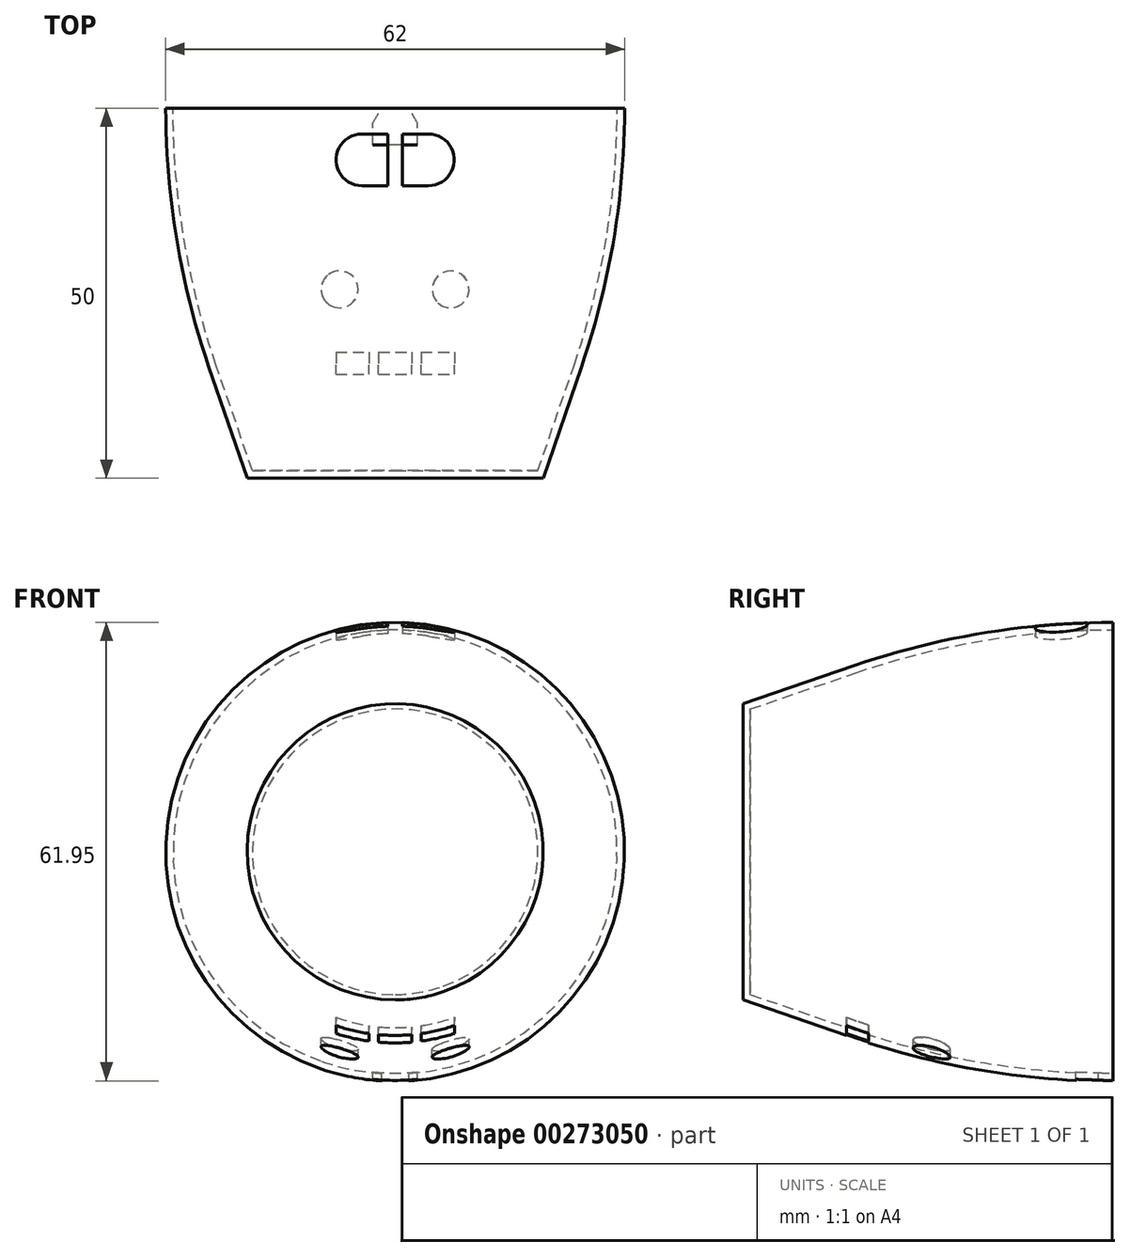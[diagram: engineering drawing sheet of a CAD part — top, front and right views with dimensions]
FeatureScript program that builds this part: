
annotation { "Feature Type Name" : "Feature", "Feature Type Description" : "" }
export const myFeature = defineFeature(function(context is Context, id is Id, definition is map)
    precondition{}
    {
        {
            var Q0;
            Q0=qCreatedBy(makeId("Right.planeOp"),FACE);
            var sketch = newSketch(context, id + "F0", { "sketchPlane" : qUnion([Q0])});
            skLineSegment(sketch, "E0", {"start": v(0, 0) * mm, "end": v(50, 0) * mm});
            skLineSegment(sketch, "E1", {"start": v(50, 0) * mm, "end": v(50, 31) * mm});
            skLineSegment(sketch, "E2", {"start": v(15, 25.15) * mm, "end": v(15, 0) * mm, "construction": true});
            skArc(sketch, "E3", {"start": v(50, 31) * mm, "mid": v(32.26, 29.53) * mm, "end": v(15, 25.15) * mm});
            skLineSegment(sketch, "E4", {"start": v(0, 0) * mm, "end": v(0, 20) * mm});
            skLineSegment(sketch, "E5", {"start": v(50, 31) * mm, "end": v(9.43, 31) * mm, "construction": true});
            skLineSegment(sketch, "E6", {"start": v(50, 0) * mm, "end": v(82.37, 0) * mm, "construction": true});
            skLineSegment(sketch, "E7", {"start": v(0, 20) * mm, "end": v(15, 25.15) * mm});
            skSolve(sketch);
        }
        {
            var Q0;
            Q0=makeQuery(id+"F0.imprint","IMPRINT",FACE,{"disambiguationData":[TD([[makeQuery(id+"F0.imprint","IMPRINT",EDGE,{"derivedFrom":sQuery(id+"F0.wireOp",EDGE,"E0")}),1.0]])]});
            var Q1;
            Q1=sQuery(id+"F0.wireOp",EDGE,"E6");
            revolve(context, id + "F1", {"entities" : qUnion([Q0]), "axis" : qUnion([Q1]), "revolveType" : RevolveType.FULL});
        }
        {
            var Q0;
            Q0=makeQuery(id+"F1.opRevolve","SWEPT_FACE",FACE,{"disambiguationData":[OSD([sQuery(id+"F0.wireOp",EDGE,"E1")])]});
            shell(context, id + "F2", {"entities" : qUnion([Q0]), "thickness" : 1 * mm});
        }
        {
            var Q0;
            Q0=qCreatedBy(makeId("Top.planeOp"),FACE);
            var sketch = newSketch(context, id + "F3", { "sketchPlane" : qUnion([Q0])});
            skLineSegment(sketch, "E8.bottom", {"start": v(-8, 17) * mm, "end": v(-3.5, 17) * mm});
            skLineSegment(sketch, "E8.top", {"start": v(-8, 14) * mm, "end": v(-3.5, 14) * mm});
            skLineSegment(sketch, "E8.left", {"start": v(-8, 17) * mm, "end": v(-8, 14) * mm});
            skLineSegment(sketch, "E8.right", {"start": v(8, 17) * mm, "end": v(8, 14) * mm});
            skPoint(sketch, "E8.middle", {"position": v(0, 15.5) * mm});
            skLineSegment(sketch, "E9", {"start": v(0, 35.5) * mm, "end": v(0, 15.5) * mm, "construction": true});
            skLineSegment(sketch, "E10", {"start": v(-7.5, 25.5) * mm, "end": v(0, 25.5) * mm, "construction": true});
            skLineSegment(sketch, "E11", {"start": v(0, 25.5) * mm, "end": v(7.5, 25.5) * mm, "construction": true});
            skCircle(sketch, "E12", {"center": v(-7.5, 25.5) * mm, "radius": 2.5 * mm});
            skCircle(sketch, "E13", {"center": v(7.5, 25.5) * mm, "radius": 2.5 * mm});
            skLineSegment(sketch, "E14.0", {"start": v(31, 50) * mm, "end": v(-31, 50) * mm, "construction": true});
            skLineSegment(sketch, "E15.left", {"start": v(3.5, 17) * mm, "end": v(3.5, 14) * mm});
            skLineSegment(sketch, "E15.right", {"start": v(2.25, 17) * mm, "end": v(2.25, 14) * mm});
            skLineSegment(sketch, "E16.left", {"start": v(-2.25, 17) * mm, "end": v(-2.25, 14) * mm});
            skLineSegment(sketch, "E16.right", {"start": v(-3.5, 17) * mm, "end": v(-3.5, 14) * mm});
            skLineSegment(sketch, "E17.trimOffspring", {"start": v(3.5, 14) * mm, "end": v(8, 14) * mm});
            skLineSegment(sketch, "E18.trimOffspring", {"start": v(-2.25, 14) * mm, "end": v(2.25, 14) * mm});
            skLineSegment(sketch, "E19.trimOffspring", {"start": v(-2.25, 17) * mm, "end": v(2.25, 17) * mm});
            skLineSegment(sketch, "E20.trimOffspring", {"start": v(3.5, 17) * mm, "end": v(8, 17) * mm});
            skLineSegment(sketch, "E21", {"start": v(3.5, 17) * mm, "end": v(2.25, 17) * mm, "construction": true});
            skLineSegment(sketch, "E22", {"start": v(-2.25, 17) * mm, "end": v(-3.5, 17) * mm, "construction": true});
            skSolve(sketch);
        }
        {
            var Q0;
            Q0 = qSketchRegion(id + "F3", true);
            extrude(context, id + "F4", {"entities" : qUnion([Q0]), "operationType" : NewBodyOperationType.REMOVE, "oppositeDirection" : true, "depth" : 100 * mm});
        }
        {
            var Q0;
            Q0=qCreatedBy(makeId("Top.planeOp"),FACE);
            var sketch = newSketch(context, id + "F5", { "sketchPlane" : qUnion([Q0])});
            skLineSegment(sketch, "E23.0", {"start": v(31, 50) * mm, "end": v(-31, 50) * mm, "construction": true});
            skLineSegment(sketch, "E24.bottom", {"start": v(-4.5, 39.5) * mm, "end": v(-1, 39.5) * mm});
            skLineSegment(sketch, "E24.top", {"start": v(-4.5, 46.5) * mm, "end": v(-1, 46.5) * mm});
            skLineSegment(sketch, "E24.left", {"start": v(-4.5, 39.5) * mm, "end": v(-4.5, 46.5) * mm, "construction": true});
            skLineSegment(sketch, "E24.right", {"start": v(4.5, 39.5) * mm, "end": v(4.5, 46.5) * mm, "construction": true});
            skPoint(sketch, "E24.middle", {"position": v(0, 43) * mm});
            skPoint(sketch, "E24.middle.positionSnap0", {"position": v(0, 50) * mm});
            skPoint(sketch, "E24.centerSnap0", {"position": v(0, 50) * mm});
            skArc(sketch, "E25", {"start": v(-4.5, 46.5) * mm, "mid": v(-8, 43) * mm, "end": v(-4.5, 39.5) * mm});
            skArc(sketch, "E26", {"start": v(4.5, 39.5) * mm, "mid": v(8, 43) * mm, "end": v(4.5, 46.5) * mm});
            skLineSegment(sketch, "E27.left", {"start": v(1, 46.5) * mm, "end": v(1, 39.5) * mm});
            skLineSegment(sketch, "E27.right", {"start": v(-1, 46.5) * mm, "end": v(-1, 39.5) * mm});
            skLineSegment(sketch, "E28.trimOffspring", {"start": v(1, 46.5) * mm, "end": v(4.5, 46.5) * mm});
            skLineSegment(sketch, "E29.trimOffspring", {"start": v(1, 39.5) * mm, "end": v(4.5, 39.5) * mm});
            skSolve(sketch);
        }
        {
            var Q0;
            Q0 = qSketchRegion(id + "F5", true);
            extrude(context, id + "F6", {"entities" : qUnion([Q0]), "operationType" : NewBodyOperationType.REMOVE, "depth" : 100 * mm});
        }
        {
            var Q0;
            Q0=qCreatedBy(makeId("Top.planeOp"),FACE);
            var sketch = newSketch(context, id + "F7", { "sketchPlane" : qUnion([Q0])});
            skLineSegment(sketch, "E30.0", {"start": v(31, 50) * mm, "end": v(-31, 50) * mm, "construction": true});
            skLineSegment(sketch, "E31.bottom", {"start": v(3, 45) * mm, "end": v(-3, 45) * mm});
            skLineSegment(sketch, "E31.top", {"start": v(3, 55) * mm, "end": v(-3, 55) * mm});
            skLineSegment(sketch, "E31.left", {"start": v(3, 45) * mm, "end": v(3, 48) * mm});
            skLineSegment(sketch, "E31.right", {"start": v(-3, 45) * mm, "end": v(-3, 48) * mm});
            skPoint(sketch, "E31.middle", {"position": v(0, 50) * mm});
            skLineSegment(sketch, "E32", {"start": v(3, 48) * mm, "end": v(1.85, 50) * mm});
            skLineSegment(sketch, "E33", {"start": v(1.85, 50) * mm, "end": v(3, 50) * mm});
            skLineSegment(sketch, "E34", {"start": v(-3, 48) * mm, "end": v(-1.85, 50) * mm});
            skLineSegment(sketch, "E35", {"start": v(-1.85, 50) * mm, "end": v(-3, 50) * mm});
            skLineSegment(sketch, "E36.trimOffspring", {"start": v(3, 50) * mm, "end": v(3, 55) * mm});
            skLineSegment(sketch, "E37.trimOffspring", {"start": v(-3, 50) * mm, "end": v(-3, 55) * mm});
            skSolve(sketch);
        }
        {
            var Q0;
            Q0 = qSketchRegion(id + "F7", true);
            extrude(context, id + "F8", {"entities" : qUnion([Q0]), "operationType" : NewBodyOperationType.REMOVE, "oppositeDirection" : true, "depth" : 100 * mm});
        }
    });
